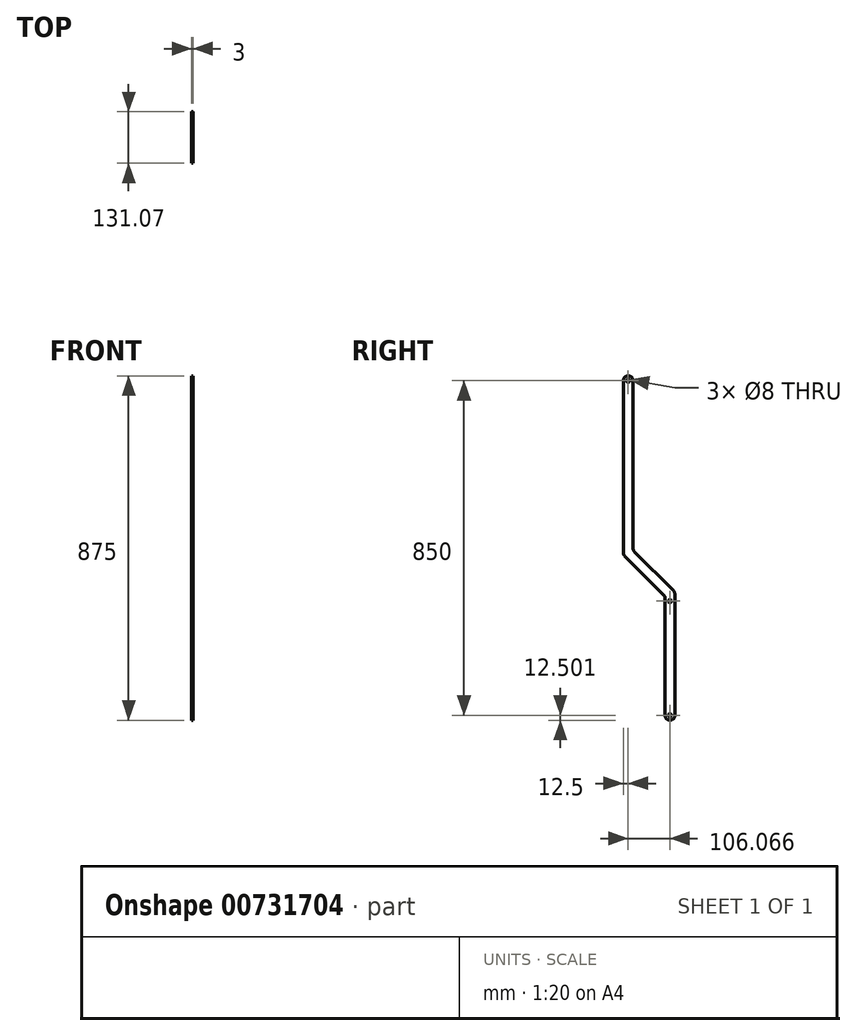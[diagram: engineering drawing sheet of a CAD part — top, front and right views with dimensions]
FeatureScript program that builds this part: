
annotation { "Feature Type Name" : "Feature", "Feature Type Description" : "" }
export const myFeature = defineFeature(function(context is Context, id is Id, definition is map)
    precondition{}
    {
        {
            var Q0;
            Q0=qCreatedBy(makeId("Right.planeOp"),FACE);
            var sketch = newSketch(context, id + "F0", { "sketchPlane" : qUnion([Q0])});
            skLineSegment(sketch, "E0.bottom", {"start": v(-122.73, -139.62) * mm, "end": v(-122.73, -139.62) * mm});
            skLineSegment(sketch, "E0.top", {"start": v(-135.23, 175.38) * mm, "end": v(-110.23, 175.38) * mm});
            skLineSegment(sketch, "E0.left", {"start": v(-135.23, -127.12) * mm, "end": v(-135.23, 175.38) * mm});
            skLineSegment(sketch, "E0.right", {"start": v(-110.23, -127.12) * mm, "end": v(-110.23, 175.38) * mm});
            skLineSegment(sketch, "E1", {"start": v(-122.73, -139.62) * mm, "end": v(-122.73, 175.38) * mm, "construction": true});
            skCircle(sketch, "E2", {"center": v(-122.73, 162.88) * mm, "radius": 4 * mm});
            skCircle(sketch, "E3", {"center": v(-122.73, -127.12) * mm, "radius": 4 * mm});
            skPoint(sketch, "E4.visualSharp", {"position": v(-135.23, -139.62) * mm});
            skArc(sketch, "E4.filletArc", {"start": v(-135.23, -127.12) * mm, "mid": v(-131.57, -135.96) * mm, "end": v(-122.73, -139.62) * mm});
            skPoint(sketch, "E5.visualSharp", {"position": v(-110.23, -139.62) * mm});
            skArc(sketch, "E5.filletArc", {"start": v(-122.73, -139.62) * mm, "mid": v(-113.9, -135.96) * mm, "end": v(-110.23, -127.12) * mm});
            skLineSegment(sketch, "E6", {"start": v(-135.23, 175.38) * mm, "end": v(-241.3, 281.45) * mm});
            skLineSegment(sketch, "E7", {"start": v(-241.3, 281.45) * mm, "end": v(-241.3, 722.88) * mm});
            skLineSegment(sketch, "E8", {"start": v(-228.8, 735.38) * mm, "end": v(-228.8, 735.38) * mm});
            skLineSegment(sketch, "E9", {"start": v(-216.3, 722.88) * mm, "end": v(-216.3, 291.8) * mm});
            skLineSegment(sketch, "E10", {"start": v(-216.3, 291.8) * mm, "end": v(-110.23, 185.74) * mm});
            skLineSegment(sketch, "E11", {"start": v(-110.23, 185.74) * mm, "end": v(-110.23, 175.38) * mm});
            skCircle(sketch, "E12", {"center": v(-228.8, 722.88) * mm, "radius": 4 * mm});
            skPoint(sketch, "E12.centerSnap0", {"position": v(-228.8, 735.38) * mm});
            skPoint(sketch, "E13.visualSharp", {"position": v(-241.3, 735.38) * mm});
            skArc(sketch, "E13.filletArc", {"start": v(-228.8, 735.38) * mm, "mid": v(-237.64, 731.72) * mm, "end": v(-241.3, 722.88) * mm});
            skPoint(sketch, "E14.visualSharp", {"position": v(-216.3, 735.38) * mm});
            skArc(sketch, "E14.filletArc", {"start": v(-216.3, 722.88) * mm, "mid": v(-219.96, 731.72) * mm, "end": v(-228.8, 735.38) * mm});
            skSolve(sketch);
        }
        {
            var Q0;
            Q0 = qSketchRegion(id + "F0", true);
            extrude(context, id + "F1", {"entities" : qUnion([Q0]), "depth" : 3 * mm, "offsetDistance" : 25 * mm});
        }
        {
            var Q0;
            Q0=makeQuery(id+"F1.opExtrude","SWEPT_EDGE",EDGE,{"disambiguationData":[OSD([sQuery(id+"F0.wireOp",EDGE,"E10"),sQuery(id+"F0.wireOp",EDGE,"E11")])]});
            var Q1;
            Q1=makeQuery(id+"F1.opExtrude","SWEPT_EDGE",EDGE,{"disambiguationData":[OSD([sQuery(id+"F0.wireOp",EDGE,"E6"),sQuery(id+"F0.wireOp",EDGE,"E7")])]});
            fillet(context, id + "F2", {"entities" : qUnion([Q0, Q1]), "radius" : 12.5 * mm, "tangentPropagation" : true, "allowEdgeOverflow" : false});
        }
        {
            var Q0;
            Q0=makeQuery(id+"F1.opExtrude","SWEPT_EDGE",EDGE,{"disambiguationData":[OSD([sQuery(id+"F0.wireOp",EDGE,"E0.top"),sQuery(id+"F0.wireOp",EDGE,"E0.left"),sQuery(id+"F0.wireOp",EDGE,"E6")])]});
            var Q1;
            Q1=makeQuery(id+"F1.opExtrude","SWEPT_EDGE",EDGE,{"disambiguationData":[OSD([sQuery(id+"F0.wireOp",EDGE,"E9"),sQuery(id+"F0.wireOp",EDGE,"E10")])]});
            fillet(context, id + "F3", {"entities" : qUnion([Q0, Q1]), "radius" : 12.5 * mm, "tangentPropagation" : true, "allowEdgeOverflow" : false});
        }
    });
